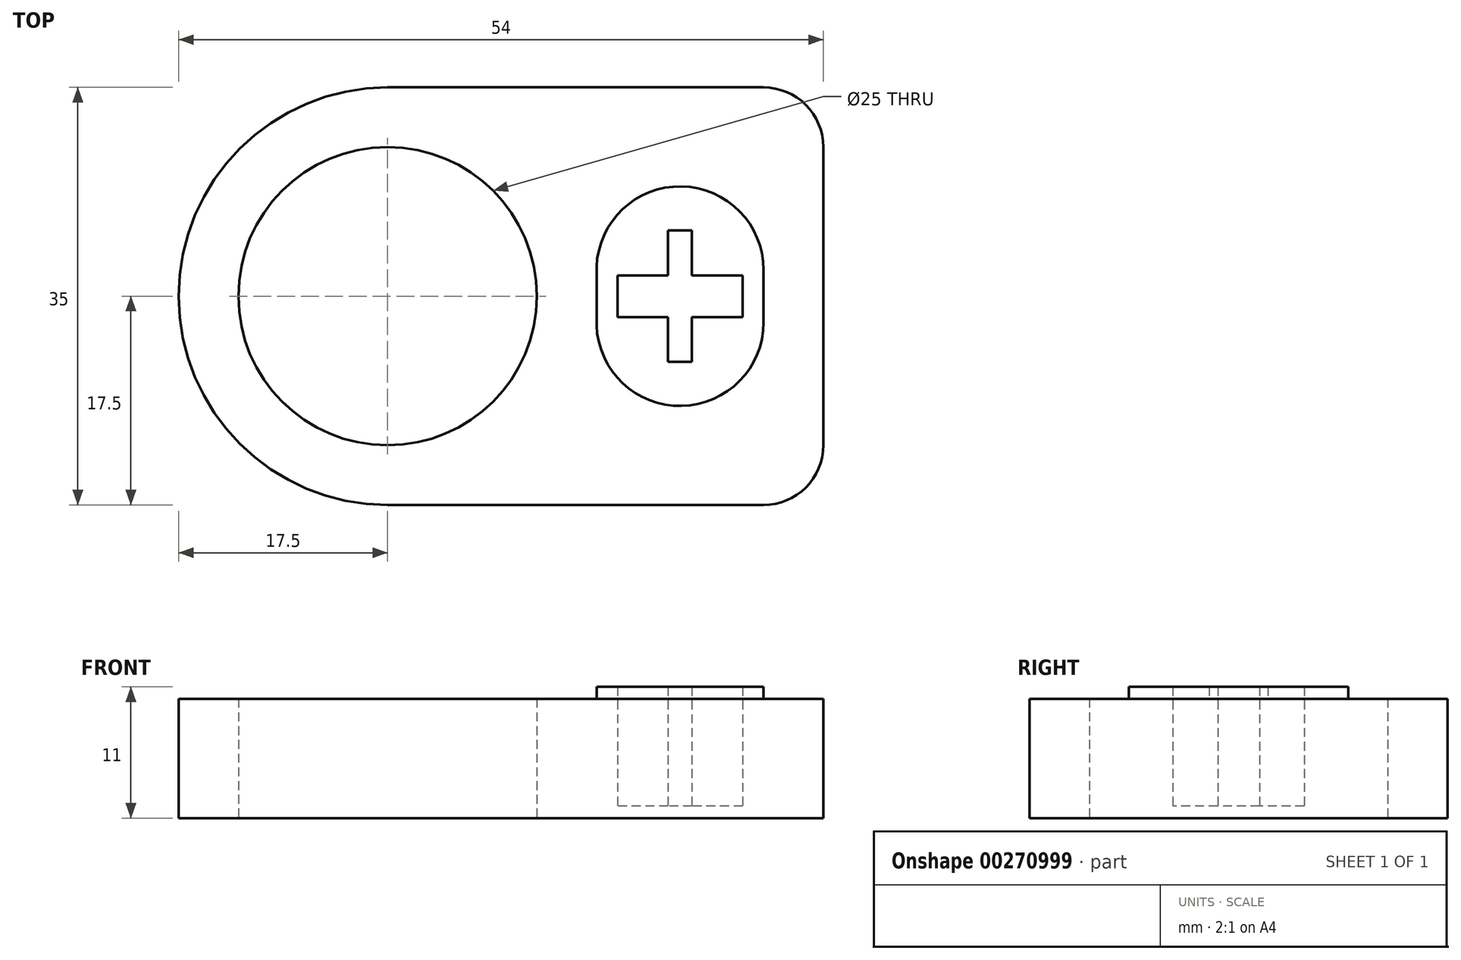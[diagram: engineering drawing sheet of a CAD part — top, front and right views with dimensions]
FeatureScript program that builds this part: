
annotation { "Feature Type Name" : "Feature", "Feature Type Description" : "" }
export const myFeature = defineFeature(function(context is Context, id is Id, definition is map)
    precondition{}
    {
        {
            var Q0;
            Q0=qCreatedBy(makeId("Top.planeOp"),FACE);
            var sketch = newSketch(context, id + "F0", { "sketchPlane" : qUnion([Q0])});
            skLineSegment(sketch, "E0.bottom", {"start": v(17.5, 0) * mm, "end": v(49, 0) * mm});
            skLineSegment(sketch, "E0.top", {"start": v(17.5, 35) * mm, "end": v(49, 35) * mm});
            skLineSegment(sketch, "E0.left", {"start": v(0, 17.5) * mm, "end": v(0, 17.5) * mm});
            skLineSegment(sketch, "E0.right", {"start": v(54, 5) * mm, "end": v(54, 30) * mm});
            skLineSegment(sketch, "E1.bottom", {"start": v(0, 0) * mm, "end": v(17.5, 0) * mm, "construction": true});
            skLineSegment(sketch, "E1.top", {"start": v(0, 17.5) * mm, "end": v(17.5, 17.5) * mm, "construction": true});
            skLineSegment(sketch, "E1.left", {"start": v(0, 0) * mm, "end": v(0, 17.5) * mm, "construction": true});
            skLineSegment(sketch, "E1.right", {"start": v(17.5, 0) * mm, "end": v(17.5, 17.5) * mm, "construction": true});
            skCircle(sketch, "E2", {"center": v(17.5, 17.5) * mm, "radius": 12.5 * mm});
            skPoint(sketch, "E3.visualSharp", {"position": v(0, 0) * mm});
            skArc(sketch, "E3.filletArc", {"start": v(0, 17.5) * mm, "mid": v(5.13, 5.13) * mm, "end": v(17.5, 0) * mm});
            skPoint(sketch, "E4.visualSharp", {"position": v(0, 35) * mm});
            skArc(sketch, "E4.filletArc", {"start": v(17.5, 35) * mm, "mid": v(5.13, 29.87) * mm, "end": v(0, 17.5) * mm});
            skPoint(sketch, "E5.visualSharp", {"position": v(54, 35) * mm});
            skArc(sketch, "E5.filletArc", {"start": v(54, 30) * mm, "mid": v(52.54, 33.54) * mm, "end": v(49, 35) * mm});
            skPoint(sketch, "E6.visualSharp", {"position": v(54, 0) * mm});
            skArc(sketch, "E6.filletArc", {"start": v(49, 0) * mm, "mid": v(52.54, 1.46) * mm, "end": v(54, 5) * mm});
            skSolve(sketch);
        }
        {
            var Q0;
            Q0=makeQuery(id+"F0.imprint","IMPRINT",FACE,{"disambiguationData":[TD([[makeQuery(id+"F0.imprint","IMPRINT",EDGE,{"derivedFrom":sQuery(id+"F0.wireOp",EDGE,"E0.bottom")}),1.0]])]});
            extrude(context, id + "F1", {"entities" : qUnion([Q0]), "depth" : 10 * mm});
        }
        {
            var Q0;
            Q0=makeQuery(id+"F1.opExtrude","CAP_FACE",FACE,{"disambiguationData":[OSD([sQuery(id+"F0.wireOp",EDGE,"E0.bottom"),sQuery(id+"F0.wireOp",EDGE,"E0.top"),sQuery(id+"F0.wireOp",EDGE,"E0.right"),sQuery(id+"F0.wireOp",EDGE,"E2"),sQuery(id+"F0.wireOp",EDGE,"E3.filletArc"),sQuery(id+"F0.wireOp",EDGE,"E4.filletArc"),sQuery(id+"F0.wireOp",EDGE,"E5.filletArc"),sQuery(id+"F0.wireOp",EDGE,"E6.filletArc")])],"isStart":false});
            var sketch = newSketch(context, id + "F2", { "sketchPlane" : qUnion([Q0])});
            skLineSegment(sketch, "E7.bottom", {"start": v(0, 0) * mm, "end": v(42, 0) * mm, "construction": true});
            skLineSegment(sketch, "E7.top", {"start": v(0, 17.5) * mm, "end": v(42, 17.5) * mm, "construction": true});
            skLineSegment(sketch, "E7.left", {"start": v(0, 0) * mm, "end": v(0, 17.5) * mm, "construction": true});
            skLineSegment(sketch, "E7.right", {"start": v(42, 0) * mm, "end": v(42, 17.5) * mm, "construction": true});
            skLineSegment(sketch, "E8", {"start": v(42, 17.5) * mm, "end": v(42, 19.7) * mm, "construction": true});
            skLineSegment(sketch, "E9", {"start": v(35, 19.96) * mm, "end": v(35, 17.5) * mm});
            skLineSegment(sketch, "E10", {"start": v(42, 17.5) * mm, "end": v(51.13, 17.5) * mm, "construction": true});
            skLineSegment(sketch, "E11", {"start": v(49, 19.7) * mm, "end": v(49, 17.5) * mm});
            skArc(sketch, "E12.trimOffspring", {"start": v(49, 19.7) * mm, "mid": v(41.87, 26.7) * mm, "end": v(35, 19.44) * mm});
            skLineSegment(sketch, "E13.MirrorCS", {"start": v(35, 15.04) * mm, "end": v(35, 17.5) * mm});
            skArc(sketch, "E14.MirrorCS", {"start": v(49, 15.3) * mm, "mid": v(41.87, 8.3) * mm, "end": v(35, 15.56) * mm});
            skLineSegment(sketch, "E15.MirrorCS", {"start": v(49, 15.3) * mm, "end": v(49, 17.5) * mm});
            skLineSegment(sketch, "E16.bottom", {"start": v(43, 23) * mm, "end": v(41, 23) * mm});
            skLineSegment(sketch, "E16.top", {"start": v(43, 12) * mm, "end": v(41, 12) * mm});
            skLineSegment(sketch, "E16.left", {"start": v(43, 23) * mm, "end": v(43, 19.25) * mm});
            skLineSegment(sketch, "E16.right", {"start": v(41, 23) * mm, "end": v(41, 19.25) * mm});
            skPoint(sketch, "E16.middle", {"position": v(42, 17.5) * mm});
            skLineSegment(sketch, "E17.bottom", {"start": v(47.25, 19.25) * mm, "end": v(43, 19.25) * mm});
            skLineSegment(sketch, "E17.top", {"start": v(47.25, 15.75) * mm, "end": v(43, 15.75) * mm});
            skLineSegment(sketch, "E17.left", {"start": v(47.25, 19.25) * mm, "end": v(47.25, 15.75) * mm});
            skLineSegment(sketch, "E17.right", {"start": v(36.75, 19.25) * mm, "end": v(36.75, 15.75) * mm});
            skPoint(sketch, "E17.cornerSnap0", {"position": v(42, 19.25) * mm});
            skLineSegment(sketch, "E18.trimOffspring", {"start": v(41, 19.25) * mm, "end": v(36.75, 19.25) * mm});
            skLineSegment(sketch, "E19.trimOffspring", {"start": v(43, 15.75) * mm, "end": v(43, 12) * mm});
            skLineSegment(sketch, "E20.trimOffspring", {"start": v(41, 15.75) * mm, "end": v(36.75, 15.75) * mm});
            skLineSegment(sketch, "E21.trimOffspring", {"start": v(41, 15.75) * mm, "end": v(41, 12) * mm});
            skSolve(sketch);
        }
        {
            var Q0;
            {var subQ10=sQuery(id+"F2.wireOp",EDGE,"E11");Q0=makeQuery(id+"F2.imprint","IMPRINT",FACE,{"disambiguationData":[TD([[makeQuery(id+"F2.imprint","IMPRINT",EDGE,{"derivedFrom":subQ10}),-1.0]])]});}
            extrude(context, id + "F3", {"entities" : qUnion([Q0]), "operationType" : NewBodyOperationType.ADD, "depth" : 1 * mm});
        }
        {
            var Q0;
            Q0=makeQuery(id+"F3.boolean.opBoolean","SPLIT",FACE,{"disambiguationData":[TD([makeQuery(id+"F3.opExtrude","SWEPT_FACE",FACE,{"disambiguationData":[OSD([sQuery(id+"F2.wireOp",EDGE,"E16.bottom")])]})])],"derivedFrom":makeQuery(id+"F1.opExtrude","CAP_FACE",FACE,{"disambiguationData":[OSD([sQuery(id+"F0.wireOp",EDGE,"E0.bottom"),sQuery(id+"F0.wireOp",EDGE,"E0.top"),sQuery(id+"F0.wireOp",EDGE,"E0.right"),sQuery(id+"F0.wireOp",EDGE,"E2"),sQuery(id+"F0.wireOp",EDGE,"E3.filletArc"),sQuery(id+"F0.wireOp",EDGE,"E4.filletArc"),sQuery(id+"F0.wireOp",EDGE,"E5.filletArc"),sQuery(id+"F0.wireOp",EDGE,"E6.filletArc")])],"isStart":false})});
            extrude(context, id + "F4", {"entities" : qUnion([Q0]), "operationType" : NewBodyOperationType.REMOVE, "oppositeDirection" : true, "depth" : 9 * mm});
        }
    });
